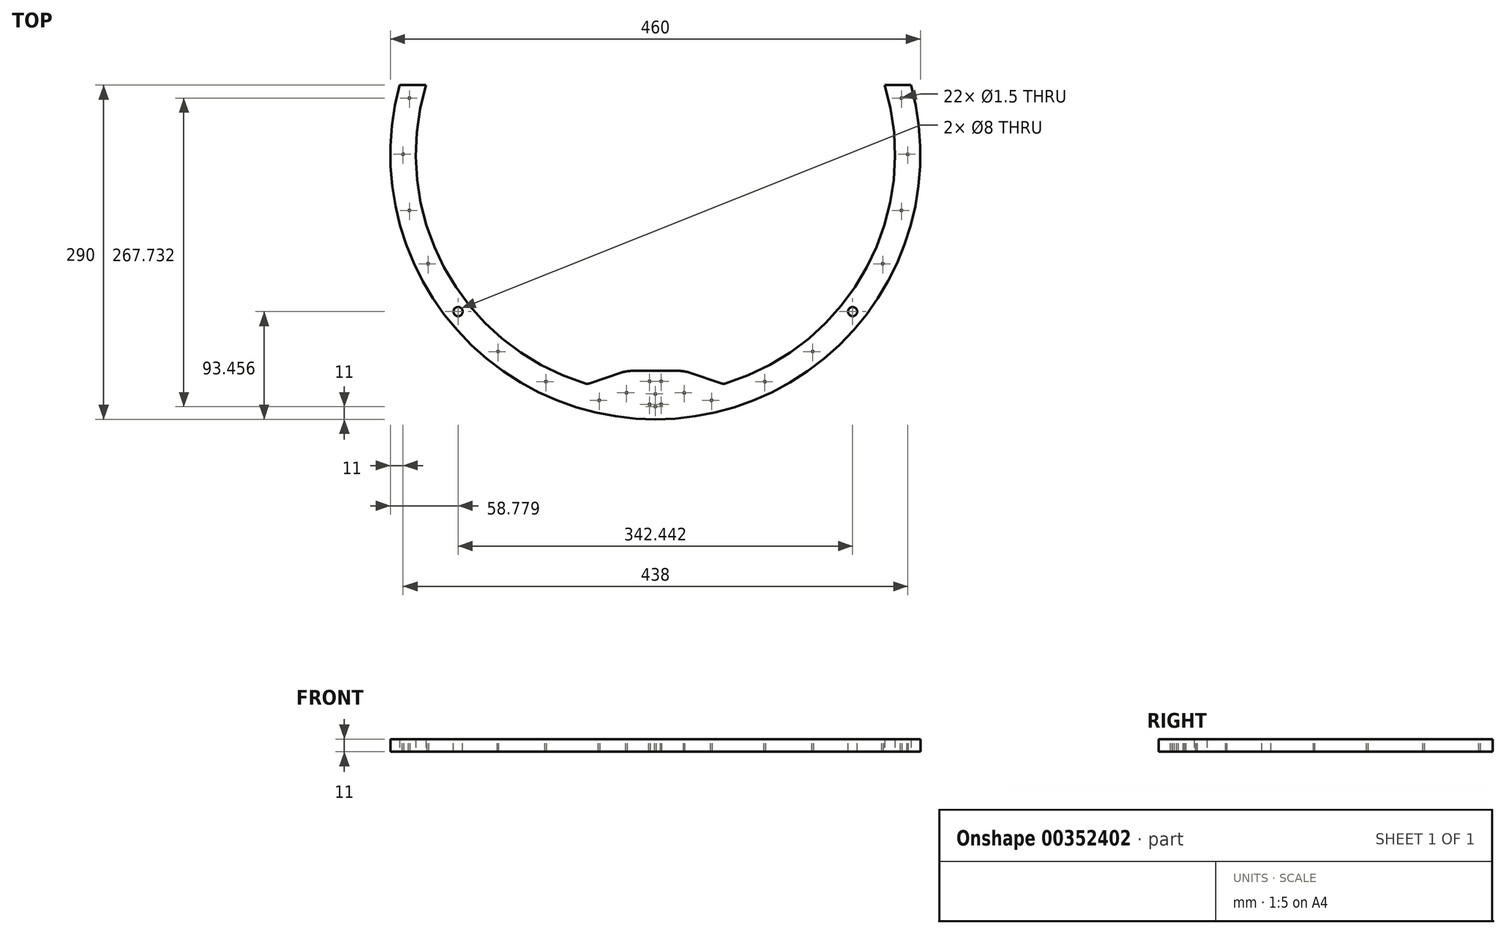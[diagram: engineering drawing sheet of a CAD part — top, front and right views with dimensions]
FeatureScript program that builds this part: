
annotation { "Feature Type Name" : "Feature", "Feature Type Description" : "" }
export const myFeature = defineFeature(function(context is Context, id is Id, definition is map)
    precondition{}
    {
        {
            var Q0;
            Q0=qCreatedBy(makeId("Top.planeOp"),FACE);
            var sketch = newSketch(context, id + "F0", { "sketchPlane" : qUnion([Q0])});
            skArc(sketch, "E0", {"start": v(-199.16, 60) * mm, "mid": v(-183.03, -98.8) * mm, "end": v(-59.12, -199.42) * mm});
            skArc(sketch, "E1", {"start": v(-222.04, 60) * mm, "mid": v(0, -230) * mm, "end": v(222.04, 60) * mm});
            skLineSegment(sketch, "E2", {"start": v(0, 0) * mm, "end": v(-114.72, 0) * mm, "construction": true});
            skLineSegment(sketch, "E3", {"start": v(0, 0) * mm, "end": v(0, 60) * mm, "construction": true});
            skLineSegment(sketch, "E4", {"start": v(199.16, 60) * mm, "end": v(222.04, 60) * mm});
            skLineSegment(sketch, "E5.MirrorCS", {"start": v(-199.16, 60) * mm, "end": v(-222.04, 60) * mm});
            skLineSegment(sketch, "E6", {"start": v(0, -208) * mm, "end": v(0, -188) * mm, "construction": true});
            skLineSegment(sketch, "E7", {"start": v(0, -188) * mm, "end": v(25, -188) * mm});
            skLineSegment(sketch, "E8", {"start": v(25, -188) * mm, "end": v(59.12, -199.42) * mm});
            skLineSegment(sketch, "E9.MirrorCS", {"start": v(0, -188) * mm, "end": v(-25, -188) * mm});
            skLineSegment(sketch, "E10.MirrorCS", {"start": v(-25, -188) * mm, "end": v(-59.12, -199.42) * mm});
            skArc(sketch, "E11.trimOffspring", {"start": v(59.12, -199.42) * mm, "mid": v(183.03, -98.8) * mm, "end": v(199.16, 60) * mm});
            skPoint(sketch, "E12.orphan", {"position": v(0, 60) * mm});
            skSolve(sketch);
        }
        {
            var Q0;
            Q0=qSketchRegion(id+"F0",true);
            extrude(context, id + "F1", {"entities" : qUnion([Q0]), "depth" : 11 * mm});
        }
        {
            var Q0;
            Q0=makeQuery(id+"F1.opExtrude","SWEPT_EDGE",EDGE,{"disambiguationData":[OSD([sQuery(id+"F0.wireOp",EDGE,"E7"),sQuery(id+"F0.wireOp",EDGE,"E8")])]});
            var Q1;
            Q1=makeQuery(id+"F1.opExtrude","SWEPT_EDGE",EDGE,{"disambiguationData":[OSD([sQuery(id+"F0.wireOp",EDGE,"E9.MirrorCS"),sQuery(id+"F0.wireOp",EDGE,"E10.MirrorCS")])]});
            fillet(context, id + "F2", {"entities" : qUnion([Q0, Q1]), "radius" : 28.52 * mm, "tangentPropagation" : true, "allowEdgeOverflow" : false});
        }
        {
            var Q0;
            Q0=makeQuery(id+"F1.opExtrude","SWEPT_EDGE",EDGE,{"disambiguationData":[OSD([sQuery(id+"F0.wireOp",EDGE,"E8"),sQuery(id+"F0.wireOp",EDGE,"E11.trimOffspring")])]});
            var Q1;
            Q1=makeQuery(id+"F1.opExtrude","SWEPT_EDGE",EDGE,{"disambiguationData":[OSD([sQuery(id+"F0.wireOp",EDGE,"E0"),sQuery(id+"F0.wireOp",EDGE,"E10.MirrorCS")])]});
            fillet(context, id + "F3", {"entities" : qUnion([Q0, Q1]), "radius" : 5 * mm, "tangentPropagation" : true, "allowEdgeOverflow" : false});
        }
        {
            var Q0;
            Q0=qCreatedBy(makeId("Top.planeOp"),FACE);
            var sketch = newSketch(context, id + "F4", { "sketchPlane" : qUnion([Q0])});
            skLineSegment(sketch, "E13", {"start": v(0, 0) * mm, "end": v(174.2, -171.38) * mm, "construction": true});
            skLineSegment(sketch, "E14", {"start": v(0, 0) * mm, "end": v(0, 36.6) * mm, "construction": true});
            skLineSegment(sketch, "E15.MirrorCS", {"start": v(0, 0) * mm, "end": v(-174.2, -171.38) * mm, "construction": true});
            skSolve(sketch);
        }
        {
            var Q0;
            Q0=makeQuery(id+"F1.opExtrude","CAP_FACE",FACE,{"disambiguationData":[OSD([sQuery(id+"F0.wireOp",EDGE,"E0"),sQuery(id+"F0.wireOp",EDGE,"E1"),sQuery(id+"F0.wireOp",EDGE,"E4"),sQuery(id+"F0.wireOp",EDGE,"E5.MirrorCS"),sQuery(id+"F0.wireOp",EDGE,"E7"),sQuery(id+"F0.wireOp",EDGE,"E8"),sQuery(id+"F0.wireOp",EDGE,"E9.MirrorCS"),sQuery(id+"F0.wireOp",EDGE,"E10.MirrorCS"),sQuery(id+"F0.wireOp",EDGE,"E11.trimOffspring")])],"isStart":false});
            var sketch = newSketch(context, id + "F5", { "sketchPlane" : qUnion([Q0])});
            skArc(sketch, "E16.0", {"start": v(-217.44, 26.07) * mm, "mid": v(0, -219) * mm, "end": v(217.44, 26.07) * mm, "construction": true});
            skCircle(sketch, "E17", {"center": v(0, -219) * mm, "radius": 0.75 * mm});
            skCircle(sketch, "E18.1.0", {"center": v(48.73, -213.5) * mm, "radius": 0.75 * mm});
            skCircle(sketch, "E18.2.0", {"center": v(95.02, -197.31) * mm, "radius": 0.75 * mm});
            skCircle(sketch, "E18.3.0", {"center": v(136.54, -171.22) * mm, "radius": 0.75 * mm});
            skCircle(sketch, "E18.4.0", {"center": v(171.22, -136.54) * mm, "radius": 0.75 * mm});
            skCircle(sketch, "E18.5.0", {"center": v(197.31, -95.02) * mm, "radius": 0.75 * mm});
            skCircle(sketch, "E18.6.0", {"center": v(213.5, -48.73) * mm, "radius": 0.75 * mm});
            skCircle(sketch, "E18.7.0", {"center": v(219, 0) * mm, "radius": 0.75 * mm});
            skCircle(sketch, "E18.8.0", {"center": v(213.5, 48.73) * mm, "radius": 0.75 * mm});
            skCircle(sketch, "E18.9.0", {"center": v(197.31, 95.02) * mm, "radius": 0.75 * mm});
            skCircle(sketch, "E18.10.0", {"center": v(171.22, 136.54) * mm, "radius": 0.75 * mm});
            skCircle(sketch, "E18.11.0", {"center": v(136.54, 171.22) * mm, "radius": 0.75 * mm});
            skCircle(sketch, "E18.12.0", {"center": v(95.02, 197.31) * mm, "radius": 0.75 * mm});
            skCircle(sketch, "E18.13.0", {"center": v(48.73, 213.5) * mm, "radius": 0.75 * mm});
            skCircle(sketch, "E18.14.0", {"center": v(0, 219) * mm, "radius": 0.75 * mm});
            skCircle(sketch, "E18.15.0", {"center": v(-48.73, 213.5) * mm, "radius": 0.75 * mm});
            skCircle(sketch, "E18.16.0", {"center": v(-95.02, 197.31) * mm, "radius": 0.75 * mm});
            skCircle(sketch, "E18.17.0", {"center": v(-136.54, 171.22) * mm, "radius": 0.75 * mm});
            skCircle(sketch, "E18.18.0", {"center": v(-171.22, 136.54) * mm, "radius": 0.75 * mm});
            skCircle(sketch, "E18.19.0", {"center": v(-197.31, 95.02) * mm, "radius": 0.75 * mm});
            skCircle(sketch, "E18.20.0", {"center": v(-213.5, 48.73) * mm, "radius": 0.75 * mm});
            skCircle(sketch, "E18.21.0", {"center": v(-219, 0) * mm, "radius": 0.75 * mm});
            skCircle(sketch, "E18.22.0", {"center": v(-213.5, -48.73) * mm, "radius": 0.75 * mm});
            skCircle(sketch, "E18.23.0", {"center": v(-197.31, -95.02) * mm, "radius": 0.75 * mm});
            skCircle(sketch, "E18.24.0", {"center": v(-171.22, -136.54) * mm, "radius": 0.75 * mm});
            skCircle(sketch, "E18.25.0", {"center": v(-136.54, -171.22) * mm, "radius": 0.75 * mm});
            skCircle(sketch, "E18.26.0", {"center": v(-95.02, -197.31) * mm, "radius": 0.75 * mm});
            skCircle(sketch, "E18.27.0", {"center": v(-48.73, -213.5) * mm, "radius": 0.75 * mm});
            skCircle(sketch, "E19", {"center": v(-5, -197) * mm, "radius": 0.75 * mm});
            skLineSegment(sketch, "E20", {"start": v(0, 0) * mm, "end": v(0, -93.12) * mm, "construction": true});
            skLineSegment(sketch, "E21", {"start": v(0, -219) * mm, "end": v(0, -197) * mm, "construction": true});
            skLineSegment(sketch, "E22", {"start": v(0, -197) * mm, "end": v(-5, -197) * mm, "construction": true});
            skCircle(sketch, "E23.MirrorC", {"center": v(5, -197) * mm, "radius": 0.75 * mm});
            skLineSegment(sketch, "E24", {"start": v(-5, -197) * mm, "end": v(-5, -217) * mm, "construction": true});
            skPoint(sketch, "E25.endSnap0", {"position": v(-5, -207) * mm});
            skLineSegment(sketch, "E26", {"start": v(-5, -207) * mm, "end": v(-25, -207) * mm, "construction": true});
            skCircle(sketch, "E27", {"center": v(0, -208) * mm, "radius": 0.75 * mm});
            skCircle(sketch, "E28.MirrorC", {"center": v(-5, -217) * mm, "radius": 0.75 * mm});
            skCircle(sketch, "E29", {"center": v(-25, -207) * mm, "radius": 0.75 * mm});
            skCircle(sketch, "E30.MirrorC", {"center": v(5, -217) * mm, "radius": 0.75 * mm});
            skCircle(sketch, "E31.MirrorC", {"center": v(25, -207) * mm, "radius": 0.75 * mm});
            skSolve(sketch);
        }
        {
            var Q0;
            Q0=qSketchRegion(id+"F5",true);
            extrude(context, id + "F6", {"entities" : qUnion([Q0]), "operationType" : NewBodyOperationType.REMOVE, "endBound" : BoundingType.THROUGH_ALL, "oppositeDirection" : true, "depth" : 25 * mm});
        }
        {
            var Q0;
            Q0=makeQuery(id+"F1.opExtrude","CAP_FACE",FACE,{"disambiguationData":[OSD([sQuery(id+"F0.wireOp",EDGE,"E0"),sQuery(id+"F0.wireOp",EDGE,"E1"),sQuery(id+"F0.wireOp",EDGE,"E4"),sQuery(id+"F0.wireOp",EDGE,"E5.MirrorCS"),sQuery(id+"F0.wireOp",EDGE,"E7"),sQuery(id+"F0.wireOp",EDGE,"E8"),sQuery(id+"F0.wireOp",EDGE,"E9.MirrorCS"),sQuery(id+"F0.wireOp",EDGE,"E10.MirrorCS"),sQuery(id+"F0.wireOp",EDGE,"E11.trimOffspring")])],"isStart":false});
            var sketch = newSketch(context, id + "F7", { "sketchPlane" : qUnion([Q0])});
            skCircle(sketch, "E32", {"center": v(-171.22, -136.54) * mm, "radius": 4 * mm});
            skLineSegment(sketch, "E33", {"start": v(0, 0) * mm, "end": v(0, -100.25) * mm, "construction": true});
            skCircle(sketch, "E34.MirrorC", {"center": v(171.22, -136.54) * mm, "radius": 4 * mm});
            skLineSegment(sketch, "E35", {"start": v(0, 0) * mm, "end": v(171.22, -136.54) * mm, "construction": true});
            skSolve(sketch);
        }
        {
            var Q0;
            Q0=qSketchRegion(id+"F7",true);
            extrude(context, id + "F8", {"entities" : qUnion([Q0]), "operationType" : NewBodyOperationType.REMOVE, "endBound" : BoundingType.THROUGH_ALL, "oppositeDirection" : true, "depth" : 25 * mm});
        }
    });
